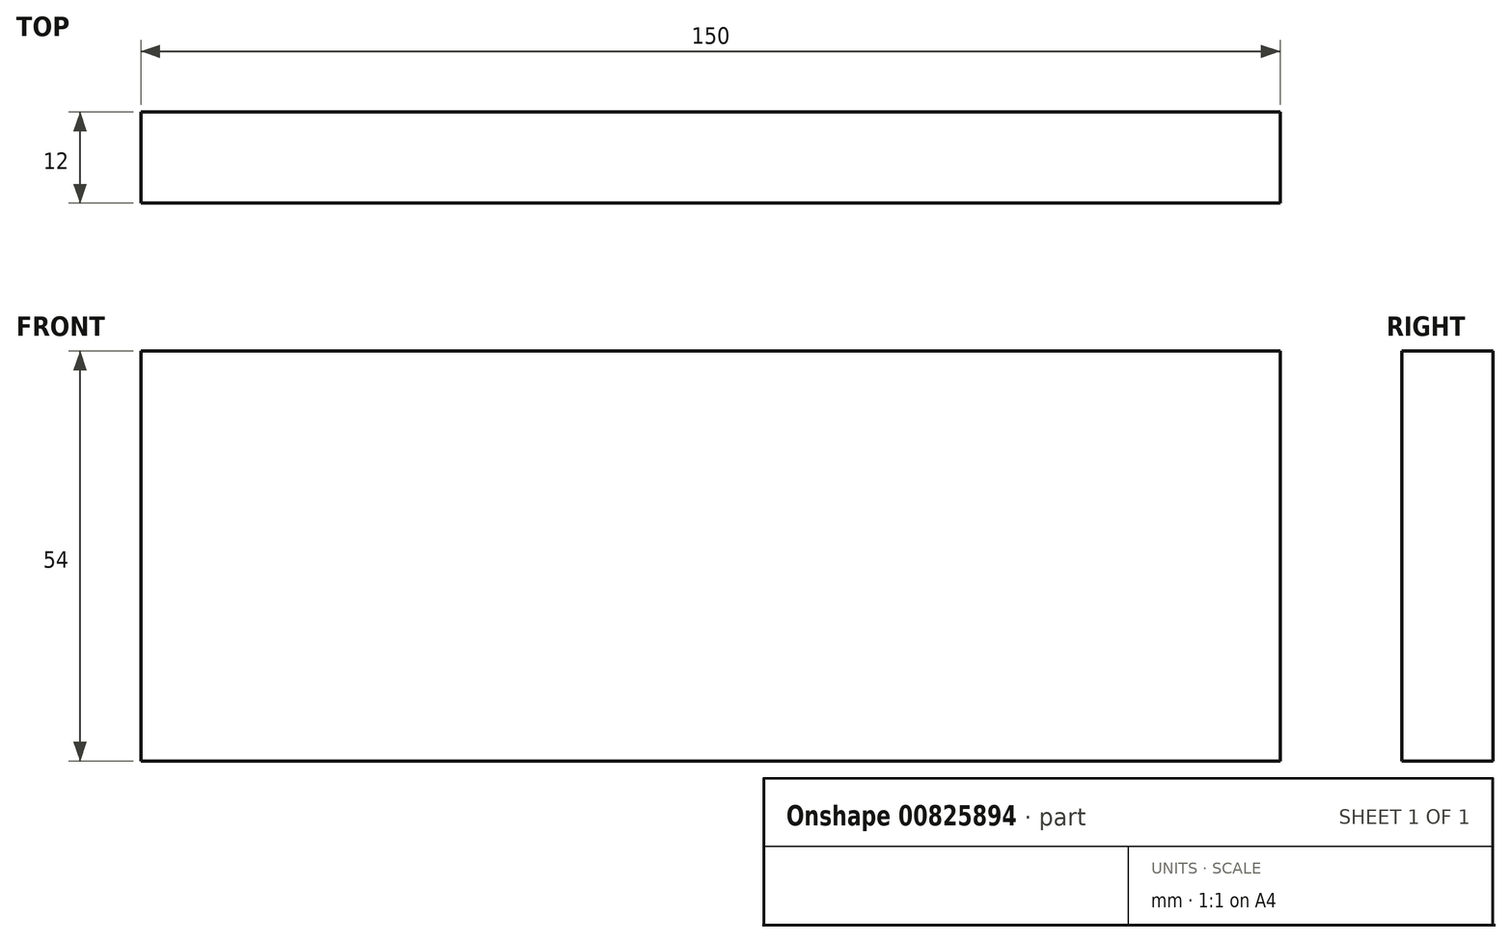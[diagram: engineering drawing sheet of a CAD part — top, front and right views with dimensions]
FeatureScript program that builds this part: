
annotation { "Feature Type Name" : "Feature", "Feature Type Description" : "" }
export const myFeature = defineFeature(function(context is Context, id is Id, definition is map)
    precondition{}
    {
        {
            var Q0;
            Q0=qCreatedBy(makeId("Right.planeOp"),FACE);
            var sketch = newSketch(context, id + "F0", { "sketchPlane" : qUnion([Q0])});
            skLineSegment(sketch, "E0.bottom", {"start": v(6, -27) * mm, "end": v(-6, -27) * mm});
            skLineSegment(sketch, "E0.top", {"start": v(6, 27) * mm, "end": v(-6, 27) * mm});
            skLineSegment(sketch, "E0.left", {"start": v(6, -27) * mm, "end": v(6, 27) * mm});
            skLineSegment(sketch, "E0.right", {"start": v(-6, -27) * mm, "end": v(-6, 27) * mm});
            skPoint(sketch, "E0.middle", {"position": v(0, 0) * mm});
            skSolve(sketch);
        }
        {
            var Q0;
            Q0=makeQuery(id+"F0.imprint","IMPRINT",FACE,{"disambiguationData":[TD([[makeQuery(id+"F0.imprint","IMPRINT",EDGE,{"derivedFrom":sQuery(id+"F0.wireOp",EDGE,"E0.bottom")}),-1.0]])]});
            extrude(context, id + "F1", {"entities" : qUnion([Q0]), "endBound" : BoundingType.SYMMETRIC, "depth" : 150 * mm, "offsetDistance" : 25.4 * mm});
        }
    });
